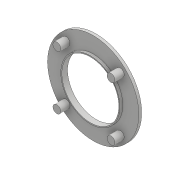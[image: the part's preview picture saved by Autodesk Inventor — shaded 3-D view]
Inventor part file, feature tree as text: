
AUTODESK INVENTOR PART (.ipt)
format: ipt  version: 2017 (Build 210142000, 142)  size: 115,200 bytes
history: native  units: mm
features: extrude x4, sketch x4, pattern_circular x1, projected_geometry x1
ambient origin geometry x8: Origin, YZ Plane, XZ Plane, XY Plane, X Axis, Y Axis, Z Axis, Center Point
bodies: Solid1 (feature_tree)
feature tree (10):
  extrude  "Extrusion1"  Depth=2.0mm TaperAngle=0.0deg
  extrude  "Extrusion2"  Depth=40.0mm
  extrude  "Extrusion3"  Depth=2.0mm TaperAngle=0.0deg
  extrude  "Extrusion4"  Depth=6.5mm
  pattern_circular  "Circular Pattern1"  [2 undecoded]
  sketch  "Sketch1"  dims[d0=64.0mm d1=2.0mm d2=0.0mm]
  sketch  "Sketch2"  dims[d3=41.5mm d4=40.0mm]
  sketch  "Sketch3"  dims[d5=2.0mm d6=0.0mm d7=2.0mm d8=0.0mm]
  projected_geometry  "Projected Loop1"
  sketch  "Sketch4"  dims[d9=5.5mm d10=19.0mm d11=19.0mm d12=6.5mm d13=0.0mm d14=40.0mm d15=360.0deg]
note: 2 required parameter values undecoded (feature->parameter linkage not recoverable at this tier; creation-order binding heuristic only, values carry confidence <= 0.55)
